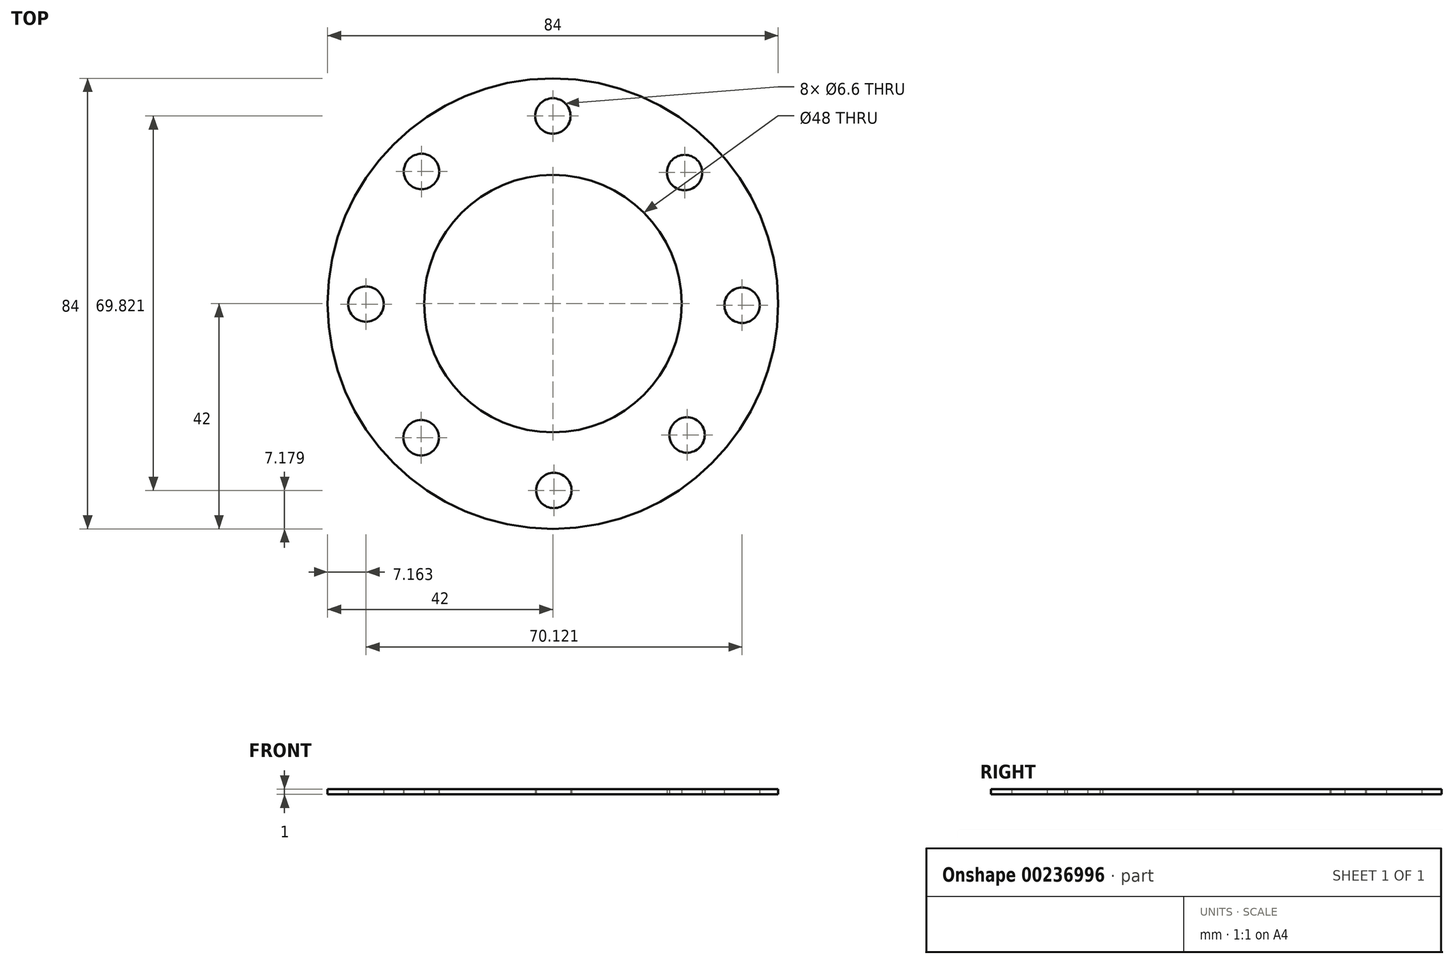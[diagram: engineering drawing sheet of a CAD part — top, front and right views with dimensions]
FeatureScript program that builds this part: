
annotation { "Feature Type Name" : "Feature", "Feature Type Description" : "" }
export const myFeature = defineFeature(function(context is Context, id is Id, definition is map)
    precondition{}
    {
        {
            var Q0;
            Q0=qCreatedBy(makeId("Top.planeOp"),FACE);
            var sketch = newSketch(context, id + "F0", { "sketchPlane" : qUnion([Q0])});
            skCircle(sketch, "E0", {"center": v(0, 0) * mm, "radius": 42 * mm});
            skCircle(sketch, "E1", {"center": v(0, 0) * mm, "radius": 24 * mm});
            skCircle(sketch, "E2.cCircle", {"center": v(0, 0) * mm, "radius": 35 * mm, "construction": true});
            skCircle(sketch, "E3", {"center": v(0, 35) * mm, "radius": 3.3 * mm});
            skCircle(sketch, "E4", {"center": v(24.56, 24.45) * mm, "radius": 3.3 * mm});
            skCircle(sketch, "E5", {"center": v(35.28, -0.28) * mm, "radius": 3.3 * mm});
            skCircle(sketch, "E6", {"center": v(25.02, -24.47) * mm, "radius": 3.3 * mm});
            skCircle(sketch, "E7", {"center": v(0.19, -34.82) * mm, "radius": 3.3 * mm});
            skCircle(sketch, "E8", {"center": v(-24.56, -25) * mm, "radius": 3.3 * mm});
            skCircle(sketch, "E9", {"center": v(-34.84, -0.08) * mm, "radius": 3.3 * mm});
            skCircle(sketch, "E10", {"center": v(-24.48, 24.65) * mm, "radius": 3.3 * mm});
            skSolve(sketch);
        }
        {
            var Q0;
            Q0 = qSketchRegion(id + "F0", true);
            extrude(context, id + "F1", {"entities" : qUnion([Q0]), "depth" : 1 * mm});
        }
    });
